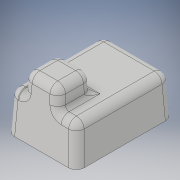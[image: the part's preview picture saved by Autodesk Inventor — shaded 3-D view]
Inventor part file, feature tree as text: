
AUTODESK INVENTOR PART (.ipt)
format: ipt  version: 2019 (Build 230136000, 136)  size: 275,968 bytes
history: native  units: mm
features: fillet x5, other x3, extrude x2, sketch x1, shell x1
ambient origin geometry x8: Origin, YZ Plane, XZ Plane, XY Plane, X Axis, Y Axis, Z Axis, Center Point
bodies: Body1 (feature_tree)
feature tree (12):
  other  "Sólido1"
  sketch  "Boceto1"  dims[d0=50.0mm d1=30.0mm d2=10.0mm d3=10.0mm d4=25.0mm d5=70.0mm d6=0.0mm d7=25.0mm d8=0.0mm d9=3.0mm d10=6.0mm d11=6.0mm d12=3.0mm d13=1.0mm d15=6.0mm d16=0.523599mm d17=0.523599mm]
  extrude  "Extrusión1"  Depth=6.0mm
  extrude  "Extrusión2"  Depth=10.0mm
  other  "Cara para el ángulo de desmoldeo2"
  other  "Cara para el ángulo de desmoldeo3"
  fillet  "Empalme1"  Radius=10.0mm
  fillet  "Empalme2"  Radius=25.0mm
  fillet  "Empalme3"  Radius=70.0mm
  fillet  "Empalme4"  Radius=25.0mm
  fillet  "Empalme5"  Radius=3.0mm
  shell  "Vaciado1"  Thickness=6.0mm
